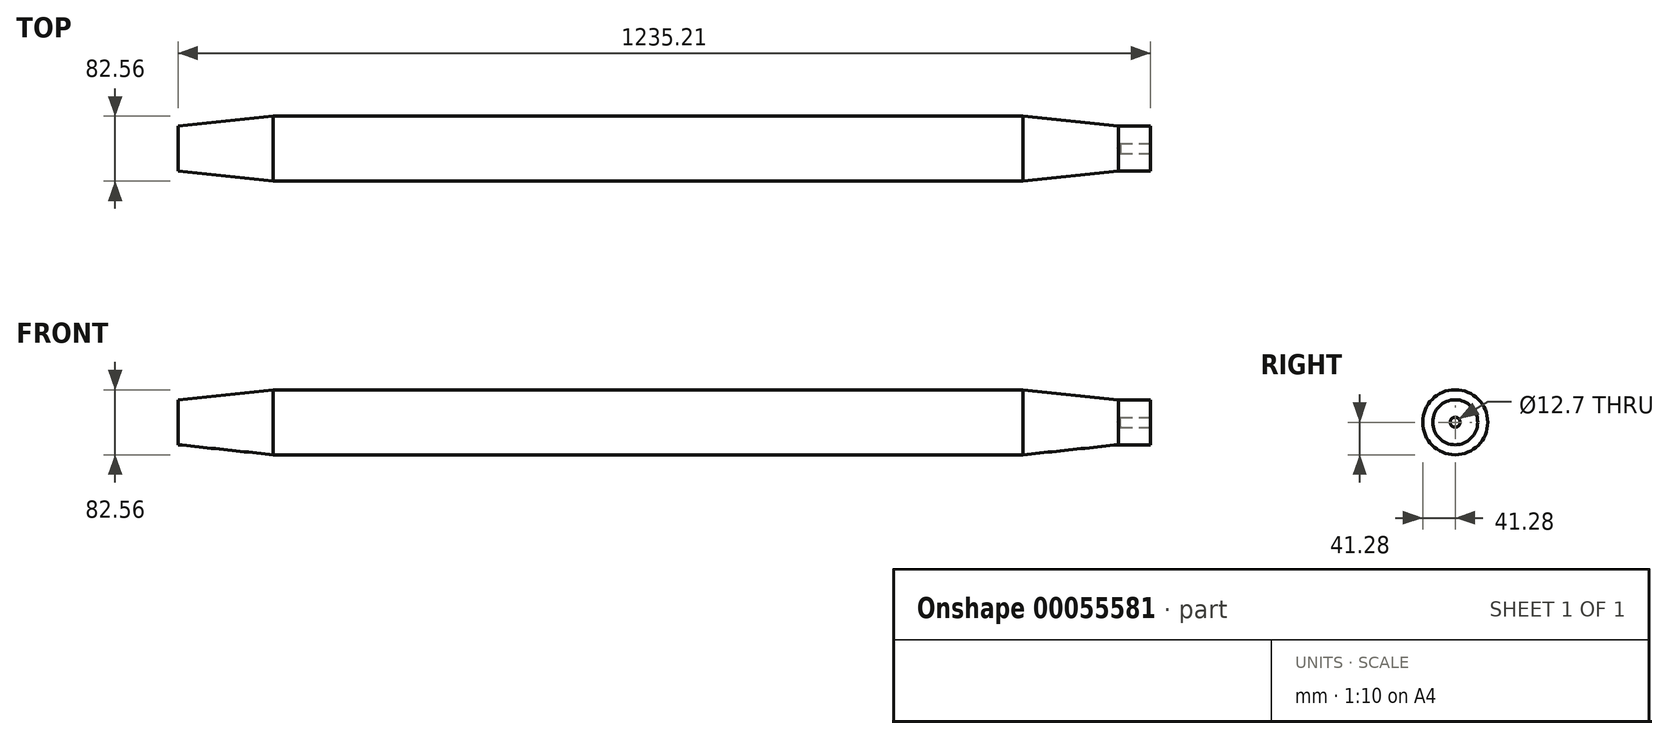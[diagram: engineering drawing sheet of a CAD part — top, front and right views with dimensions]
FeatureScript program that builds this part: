
annotation { "Feature Type Name" : "Feature", "Feature Type Description" : "" }
export const myFeature = defineFeature(function(context is Context, id is Id, definition is map)
    precondition{}
    {
        {
            var Q0;
            Q0=qCreatedBy(makeId("Right.planeOp"),FACE);
            var sketch = newSketch(context, id + "F0", { "sketchPlane" : qUnion([Q0])});
            skCircle(sketch, "E0", {"center": v(0, 0) * mm, "radius": 41.28 * mm});
            skSolve(sketch);
        }
        {
            var Q0;
            Q0=qSketchRegion(id+"F0",true);
            extrude(context, id + "F1", {"entities" : qUnion([Q0]), "endBound" : BoundingType.SYMMETRIC, "depth" : 952.5 * mm});
        }
        {
            var Q0;
            Q0=qCreatedBy(makeId("Right.planeOp"),FACE);
            cPlane(context, id + "F2", {"entities" : qUnion([Q0]), "cplaneType" : CPlaneType.OFFSET, "offset" : 638.17 * mm, "width" : 152.4 * mm, "height" : 152.4 * mm});
        }
        {
            var Q0;
            Q0=qCreatedBy(id+"F2.planeOp",FACE);
            var sketch = newSketch(context, id + "F3", { "sketchPlane" : qUnion([Q0])});
            skCircle(sketch, "E1", {"center": v(0, 0) * mm, "radius": 28.57 * mm});
            skSolve(sketch);
        }
        {
            var Q0;
            Q0=qSketchRegion(id+"F3",true);
            extrude(context, id + "F4", {"entities" : qUnion([Q0]), "oppositeDirection" : true, "depth" : 41.15 * mm});
        }
        {
            var Q0;
            Q0=makeQuery(id+"F1.opExtrude","CAP_FACE",FACE,{"disambiguationData":[OSD([sQuery(id+"F0.wireOp",EDGE,"E0")])],"isStart":false});
            var Q1;
            Q1=makeQuery(id+"F4.opExtrude","CAP_FACE",FACE,{"disambiguationData":[OSD([sQuery(id+"F3.wireOp",EDGE,"E1")])],"isStart":false});
            loft(context, id + "F5", {"sheetProfilesArray" : [{ "sheetProfileEntities" : qUnion([Q0]) }, { "sheetProfileEntities" : qUnion([Q1]) }]});
        }
        {
            var Q0;
            Q0=makeQuery(id+"F5.opLoft","SWEPT_BODY",BODY,{"disambiguationData":[OSD([sQuery(id+"F0.wireOp",EDGE,"E0"),sQuery(id+"F3.wireOp",EDGE,"E1")])]});
            var Q1;
            Q1=qCreatedBy(makeId("Right.planeOp"),FACE);
            mirror(context, id + "F6", {"operationType" : NewBodyOperationType.ADD, "entities" : qUnion([Q0]), "mirrorPlane" : qUnion([Q1])});
        }
        {
            var Q0;
            Q0=qCreatedBy(id+"F2.planeOp",FACE);
            var sketch = newSketch(context, id + "F7", { "sketchPlane" : qUnion([Q0])});
            skPoint(sketch, "E2", {"position": v(0, 0) * mm});
            skSolve(sketch);
        }
        {
            var Q0;
            Q0=makeQuery(id+"F6.opPattern","COPY",FACE,{"derivedFrom":makeQuery(id+"F4.opExtrude","CAP_FACE",FACE,{"disambiguationData":[OSD([sQuery(id+"F3.wireOp",EDGE,"E1")])],"isStart":true}),"instanceName":"1"});
            var sketch = newSketch(context, id + "F8", { "sketchPlane" : qUnion([Q0])});
            skPoint(sketch, "E3", {"position": v(0, 0) * mm});
            skSolve(sketch);
        }
        {
            var Q0;
            Q0=sQuery(id+"F8.wireOp",VERTEX,"E3");
            var Q1;
            Q1=sQuery(id+"F7.wireOp",VERTEX,"E2");
            var Q2;
            Q2=makeQuery(id+"F1.opExtrude","SWEPT_BODY",BODY,{"disambiguationData":[OSD([sQuery(id+"F0.wireOp",EDGE,"E0")])]});
            hole(context, id + "F9", {"style" : HoleStyle.SIMPLE, "holeDiameter" : 12.7 * mm, "endStyle" : HoleEndStyle.BLIND, "holeDepth" : 38.1 * mm, "locations" : qUnion([Q0, Q1]), "scope" : qUnion([Q2])});
        }
    });
